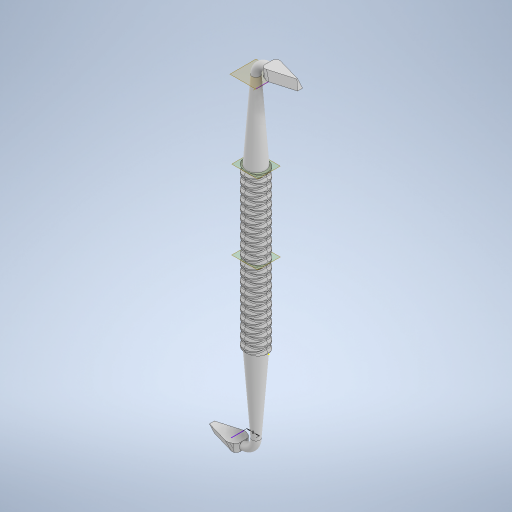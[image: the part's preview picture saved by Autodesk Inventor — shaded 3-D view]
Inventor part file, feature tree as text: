
AUTODESK INVENTOR PART (.ipt)
format: ipt  version: 2024 (Build 280153000, 153)  size: 2,777,088 bytes
history: native  units: mm
features: chamfer x16, sketch x16, extrude x7, helix x4, plane x3, revolve x2, fillet x2, other x1
ambient origin geometry x8: Origin, YZ Plane, XZ Plane, XY Plane, X Axis, Y Axis, Z Axis, Center Point
bodies: Solid1 (feature_tree)
feature tree (51):
  extrude  "Extrusion1"  Depth=100.0mm TaperAngle=0.0deg
  helix  "Coil1"  [1 undecoded]
  helix  "Coil2"  [1 undecoded]
  helix  "Coil3"  [1 undecoded]
  helix  "Coil4"  [1 undecoded]
  chamfer  "Chamfer1"  Distance=1.0mm Angle=45.0deg
  chamfer  "Chamfer2"  Distance=1.0mm Angle=45.0deg
  chamfer  "Chamfer3"  Distance=1.0mm Angle=45.0deg
  chamfer  "Chamfer4"  Distance=1.0mm Angle=45.0deg
  chamfer  "Chamfer5"  Distance=1.0mm Angle=45.0deg
  chamfer  "Chamfer6"  Distance=1.0mm Angle=45.0deg
  chamfer  "Chamfer7"  Distance=1.0mm Angle=45.0deg
  chamfer  "Chamfer8"  Distance=50.0mm
  extrude  "Extrusion2"  TaperAngle=90.0deg  [1 undecoded]
  chamfer  "Chamfer9"  Distance=50.0mm
  sketch  "Sketch9"  dims[d65=50.0mm d66=50.0mm d67=0.698132mm d68=90.0deg]
  plane  "Work Plane3"
  sketch  "Sketch10"  dims[d69=-50.0mm]
  other  "Work Axis2"
  revolve  "Revolution1"  [1 undecoded]
  plane  "Work Plane4"
  plane  "Work Plane5"
  extrude  "Extrusion3"  Depth=20.0mm TaperAngle=0.0deg
  chamfer  "Chamfer10"  Distance=20.0mm
  sketch  "Sketch12"  dims[d71=12.0mm d72=50.0mm d73=0.0mm]
  revolve  "Revolution2"  [1 undecoded]
  sketch  "Sketch14"  dims[d78=90.0deg d79=20.0mm d80=0.0mm]
  extrude  "Extrusion4"  Depth=3.0mm
  extrude  "Extrusion5"  Depth=3.0mm TaperAngle=0.0deg
  extrude  "Extrusion6"  Depth=3.0mm
  extrude  "Extrusion7"  Depth=3.0mm
  chamfer  "Chamfer11"  Distance=5.0mm
  chamfer  "Chamfer12"  Distance=3.0mm
  chamfer  "Chamfer13"  Distance=5.0mm
  fillet  "Fillet1"  Radius=5.0mm
  chamfer  "Chamfer14"  Distance=5.0mm
  chamfer  "Chamfer15"  Distance=3.0mm
  chamfer  "Chamfer16"  [1 undecoded]
  fillet  "Fillet2"  [1 undecoded]
  sketch  "Sketch1"  dims[d0=15.0mm d1=100.0mm d2=0.0mm d3=2.0mm]
  sketch  "Sketch2"  dims[d4=10.0mm d5=10.0mm d6=100.0mm d7=0.0mm d8=90.0deg d9=90.0deg d10=0.0mm d11=0.0mm]
  sketch  "Sketch4"  dims[d12=10.0mm d13=10.0mm d14=100.0mm d15=0.0mm d16=90.0deg d17=90.0deg d18=0.0mm d19=0.0mm d20=2.0mm]
  sketch  "Sketch5"  dims[d21=10.0mm d22=10.0mm d23=100.0mm d24=0.0mm d25=90.0deg d26=90.0deg d27=0.0mm d28=0.0mm d29=2.0mm]
  sketch  "Sketch6"  dims[d30=10.0mm d31=10.0mm d32=100.0mm d33=0.0mm d34=90.0deg d35=90.0deg d36=0.0mm d37=0.0mm d38=1.0mm d39=2.0mm d40=45.0deg d41=1.0mm d42=2.0mm d43=45.0deg d44=1.0mm d45=2.0mm d46=45.0deg d47=1.0mm d48=2.0mm d49=45.0deg d50=1.0mm d51=2.0mm d52=45.0deg d53=1.0mm d54=2.0mm d55=45.0deg d56=1.0mm d57=2.0mm d58=45.0deg d59=1.0mm d60=2.0mm d61=45.0deg]
  sketch  "Sketch8"  dims[d62=12.0mm d63=50.0mm d64=0.0mm]
  sketch  "Sketch11"  dims[d70=-100.0mm]
  sketch  "Sketch13"  dims[d74=50.0mm d75=50.0mm d76=0.698132mm d77=8.0mm]
  sketch  "Sketch15"  dims[d81=5.0mm]
  sketch  "Sketch16"  dims[d82=5.0mm d85=20.0mm d86=0.0mm]
  sketch  "Sketch17"  dims[d87=12.0mm d88=5.007mm]
  sketch  "Sketch18"  dims[d89=20.0mm d90=0.0mm d91=5.0mm d92=20.0mm d93=0.0mm d94=5.0mm d95=2.0mm d96=3.490659mm d97=5.0mm d98=2.0mm d99=3.490659mm d100=5.0mm d101=2.0mm d102=3.490659mm d103=3.0mm d104=5.0mm d105=2.0mm d106=3.490659mm d107=5.0mm d108=2.0mm d109=3.490659mm d110=5.0mm d111=2.0mm d112=3.490659mm d113=3.0mm]
note: 9 required parameter values undecoded (feature->parameter linkage not recoverable at this tier; creation-order binding heuristic only, values carry confidence <= 0.55)